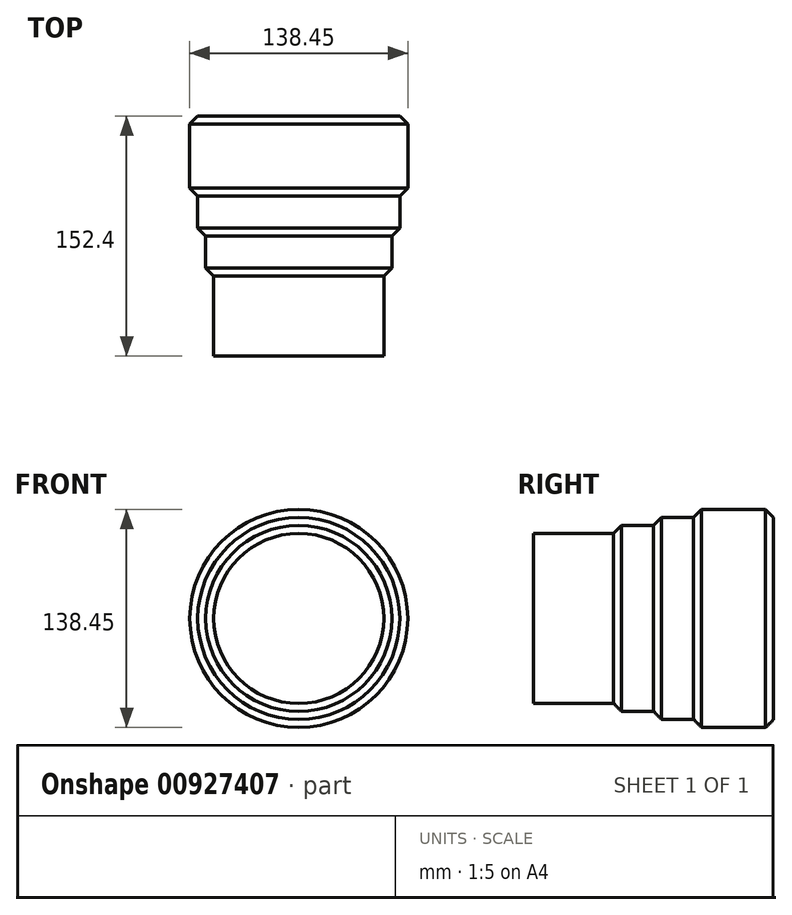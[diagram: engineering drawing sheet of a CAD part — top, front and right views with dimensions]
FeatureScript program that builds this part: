
annotation { "Feature Type Name" : "Feature", "Feature Type Description" : "" }
export const myFeature = defineFeature(function(context is Context, id is Id, definition is map)
    precondition{}
    {
        {
            var Q0;
            Q0=qCreatedBy(makeId("Front.planeOp"),FACE);
            var sketch = newSketch(context, id + "F0", { "sketchPlane" : qUnion([Q0])});
            skCircle(sketch, "E0", {"center": v(-16.03, 36.59) * mm, "radius": 69.22 * mm});
            skSolve(sketch);
        }
        {
            var Q0;
            Q0=makeQuery(id+"F0.imprint","IMPRINT",FACE,{"disambiguationData":[TD([[makeQuery(id+"F0.imprint","IMPRINT",EDGE,{"derivedFrom":sQuery(id+"F0.wireOp",EDGE,"E0")}),1.0]])]});
            extrude(context, id + "F1", {"entities" : qUnion([Q0]), "depth" : 50.8 * mm, "offsetDistance" : 25.4 * mm});
        }
        {
            var Q0;
            Q0=makeQuery(id+"F1.opExtrude","SWEPT_FACE",FACE,{"disambiguationData":[OSD([sQuery(id+"F0.wireOp",EDGE,"E0")])]});
            var Q1;
            Q1=makeQuery(id+"F1.opExtrude","CAP_FACE",FACE,{"disambiguationData":[OSD([sQuery(id+"F0.wireOp",EDGE,"E0")])],"isStart":false});
            chamfer(context, id + "F2", {"entities" : qUnion([Q0, Q1]), "width" : 5.08 * mm, "tangentPropagation" : true});
        }
        {
            var Q0;
            Q0=makeQuery(id+"F1.opExtrude","CAP_FACE",FACE,{"disambiguationData":[OSD([sQuery(id+"F0.wireOp",EDGE,"E0")])],"isStart":false});
            extrude(context, id + "F3", {"entities" : qUnion([Q0]), "operationType" : NewBodyOperationType.ADD, "depth" : 25.4 * mm, "offsetDistance" : 25.4 * mm});
        }
        {
            var Q0;
            Q0=makeQuery(id+"F3.opExtrude","CAP_FACE",FACE,{"disambiguationData":[OSD([sQuery(id+"F0.wireOp",EDGE,"E0")])],"isStart":false});
            chamfer(context, id + "F4", {"entities" : qUnion([Q0]), "width" : 5.08 * mm, "tangentPropagation" : true});
        }
        {
            var Q0;
            Q0=makeQuery(id+"F3.opExtrude","CAP_FACE",FACE,{"disambiguationData":[OSD([sQuery(id+"F0.wireOp",EDGE,"E0")])],"isStart":false});
            extrude(context, id + "F5", {"entities" : qUnion([Q0]), "operationType" : NewBodyOperationType.ADD, "depth" : 25.4 * mm, "offsetDistance" : 25.4 * mm});
        }
        {
            var Q0;
            Q0=makeQuery(id+"F5.opExtrude","CAP_FACE",FACE,{"disambiguationData":[OSD([sQuery(id+"F0.wireOp",EDGE,"E0")])],"isStart":false});
            chamfer(context, id + "F6", {"entities" : qUnion([Q0]), "width" : 5.08 * mm, "tangentPropagation" : true});
        }
        {
            var Q0;
            Q0=makeQuery(id+"F5.opExtrude","CAP_FACE",FACE,{"disambiguationData":[OSD([sQuery(id+"F0.wireOp",EDGE,"E0")])],"isStart":false});
            extrude(context, id + "F7", {"entities" : qUnion([Q0]), "operationType" : NewBodyOperationType.ADD, "depth" : 50.8 * mm, "offsetDistance" : 25.4 * mm});
        }
    });
